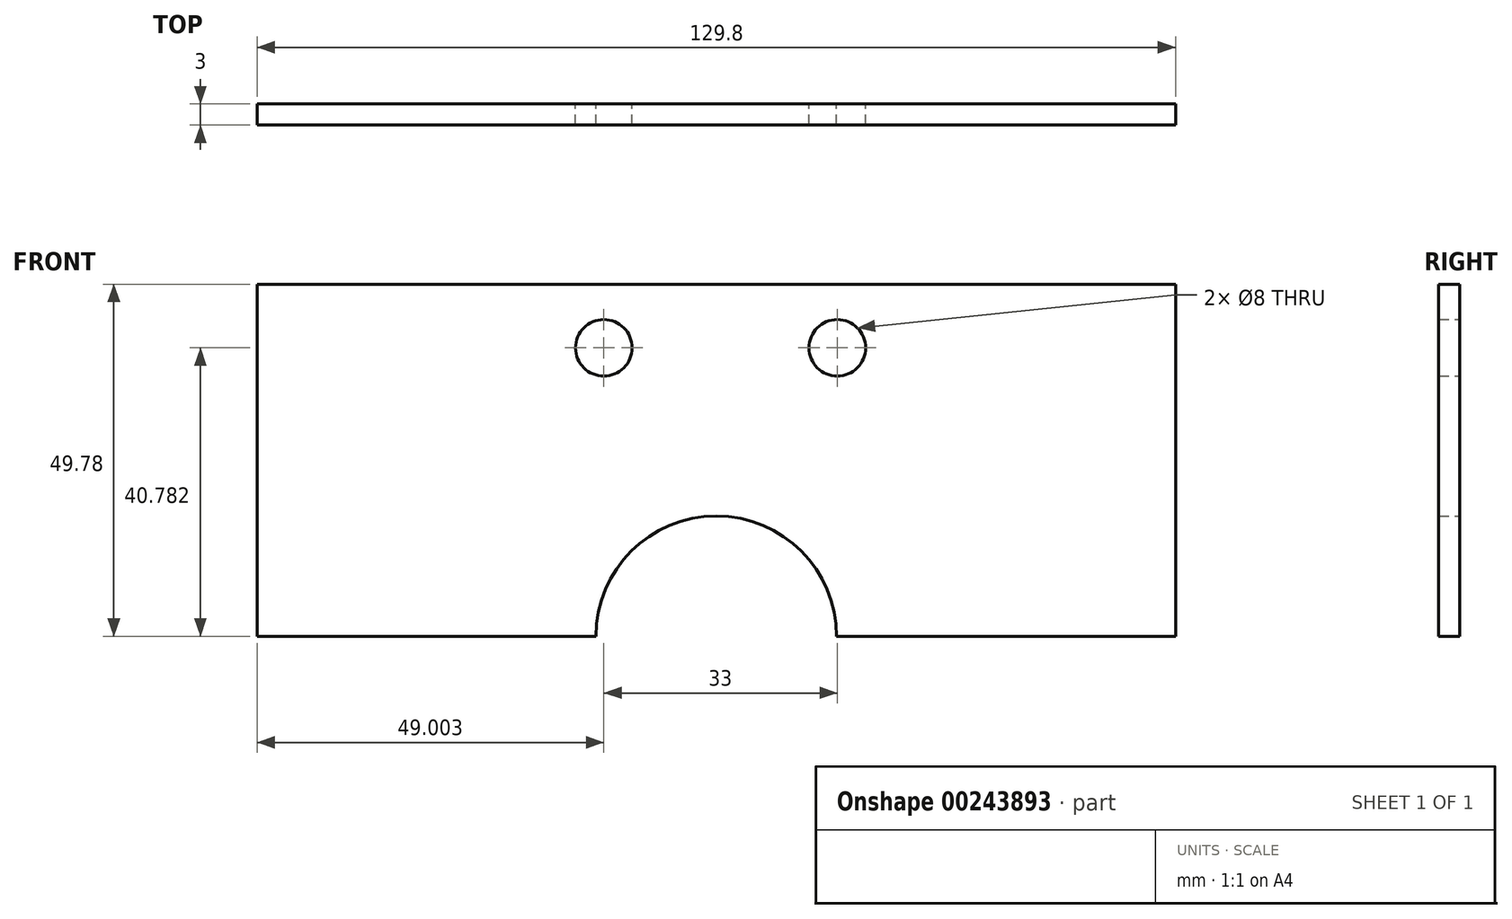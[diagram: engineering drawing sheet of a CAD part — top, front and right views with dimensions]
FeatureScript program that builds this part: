
annotation { "Feature Type Name" : "Feature", "Feature Type Description" : "" }
export const myFeature = defineFeature(function(context is Context, id is Id, definition is map)
    precondition{}
    {
        {
            var Q0;
            Q0=qCreatedBy(makeId("Front.planeOp"),FACE);
            var sketch = newSketch(context, id + "F0", { "sketchPlane" : qUnion([Q0])});
            skLineSegment(sketch, "E0.bottom", {"start": v(-64.9, -24.9) * mm, "end": v(64.9, -24.9) * mm});
            skLineSegment(sketch, "E0.top", {"start": v(-64.9, 24.9) * mm, "end": v(64.9, 24.9) * mm});
            skLineSegment(sketch, "E0.left", {"start": v(-64.9, -24.9) * mm, "end": v(-64.9, 24.9) * mm});
            skLineSegment(sketch, "E0.right", {"start": v(64.9, -24.9) * mm, "end": v(64.9, 24.9) * mm});
            skPoint(sketch, "E0.middle", {"position": v(0, 0) * mm});
            skCircle(sketch, "E1", {"center": v(-15.9, 15.9) * mm, "radius": 4 * mm});
            skCircle(sketch, "E2", {"center": v(17.1, 15.9) * mm, "radius": 4 * mm});
            skArc(sketch, "E3", {"start": v(17, -24.9) * mm, "mid": v(0, -7.9) * mm, "end": v(-17, -24.9) * mm});
            skSolve(sketch);
        }
        {
            var Q0;
            Q0=makeQuery(id+"F0.imprint","IMPRINT",FACE,{"disambiguationData":[TD([[makeQuery(id+"F0.imprint","IMPRINT",EDGE,{"derivedFrom":sQuery(id+"F0.wireOp",EDGE,"E0.bottom")}),1.0]])]});
            extrude(context, id + "F1", {"entities" : qUnion([Q0]), "endBound" : BoundingType.SYMMETRIC, "depth" : 3 * mm});
        }
    });
